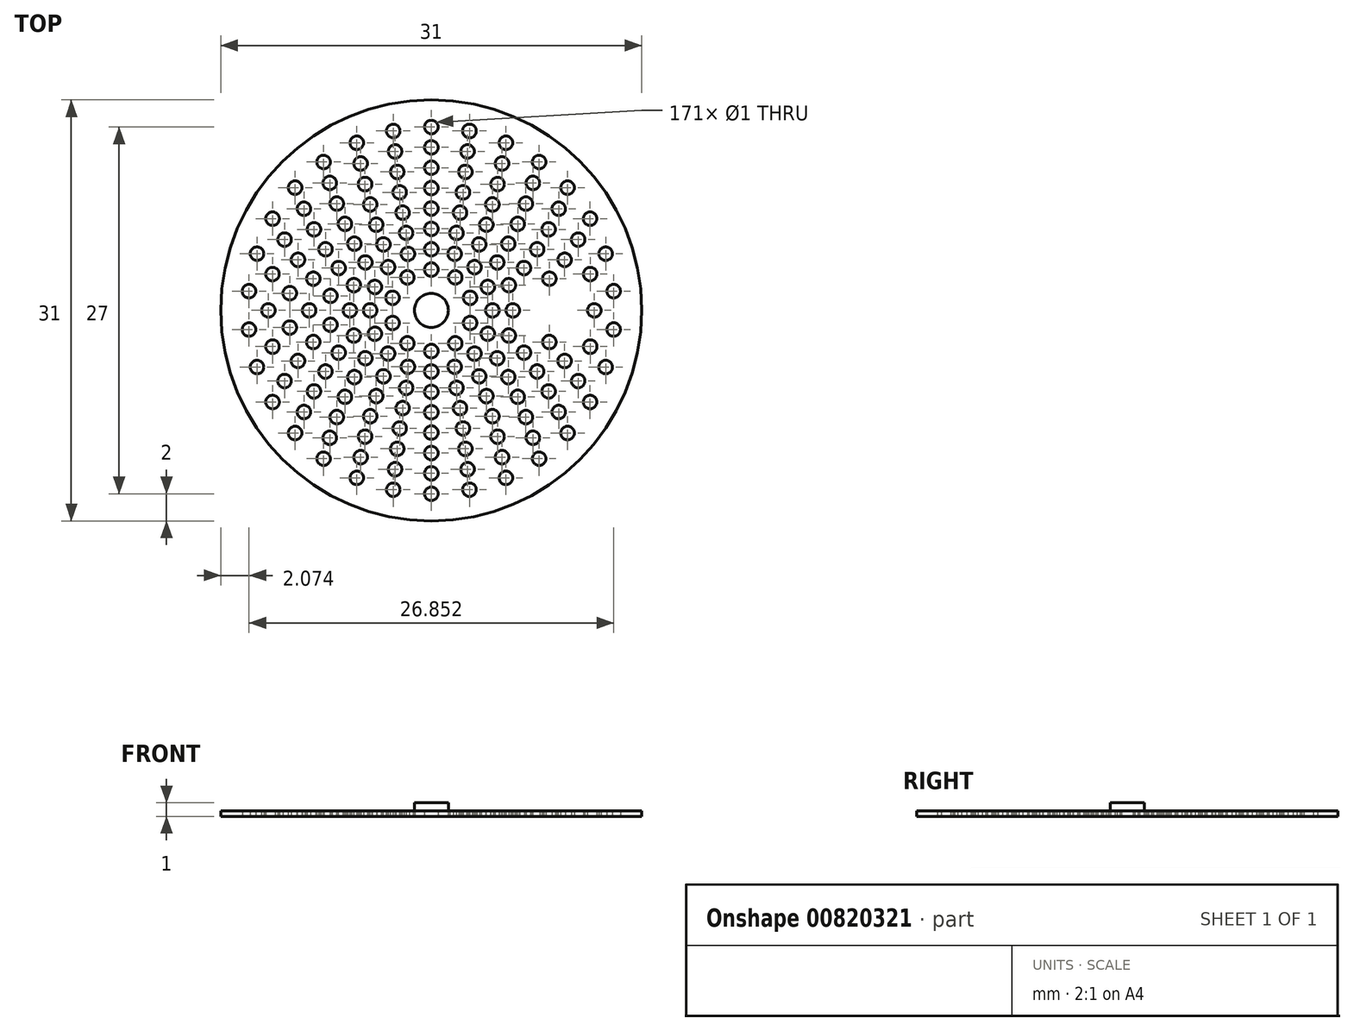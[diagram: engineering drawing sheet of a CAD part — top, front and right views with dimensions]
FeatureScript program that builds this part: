
annotation { "Feature Type Name" : "Feature", "Feature Type Description" : "" }
export const myFeature = defineFeature(function(context is Context, id is Id, definition is map)
    precondition{}
    {
        {
            var Q0;
            Q0=qCreatedBy(makeId("Top.planeOp"),FACE);
            var sketch = newSketch(context, id + "F0", { "sketchPlane" : qUnion([Q0])});
            skCircle(sketch, "E0", {"center": v(0, 0) * mm, "radius": 15.5 * mm});
            skCircle(sketch, "E1", {"center": v(0, 13.5) * mm, "radius": 0.5 * mm});
            skCircle(sketch, "E2.1.0", {"center": v(-2.8, 13.2) * mm, "radius": 0.5 * mm});
            skCircle(sketch, "E2.2.0", {"center": v(-5.5, 12.33) * mm, "radius": 0.5 * mm});
            skCircle(sketch, "E2.3.0", {"center": v(-7.94, 10.92) * mm, "radius": 0.5 * mm});
            skCircle(sketch, "E2.4.0", {"center": v(-10.03, 9.03) * mm, "radius": 0.5 * mm});
            skCircle(sketch, "E2.5.0", {"center": v(-11.7, 6.75) * mm, "radius": 0.5 * mm});
            skCircle(sketch, "E2.6.0", {"center": v(-12.84, 4.17) * mm, "radius": 0.5 * mm});
            skCircle(sketch, "E2.7.0", {"center": v(-13.43, 1.41) * mm, "radius": 0.5 * mm});
            skCircle(sketch, "E2.8.0", {"center": v(-13.43, -1.41) * mm, "radius": 0.5 * mm});
            skCircle(sketch, "E2.9.0", {"center": v(-12.84, -4.17) * mm, "radius": 0.5 * mm});
            skCircle(sketch, "E2.10.0", {"center": v(-11.7, -6.75) * mm, "radius": 0.5 * mm});
            skCircle(sketch, "E2.11.0", {"center": v(-10.03, -9.03) * mm, "radius": 0.5 * mm});
            skCircle(sketch, "E2.12.0", {"center": v(-7.94, -10.92) * mm, "radius": 0.5 * mm});
            skCircle(sketch, "E2.13.0", {"center": v(-5.5, -12.33) * mm, "radius": 0.5 * mm});
            skCircle(sketch, "E2.14.0", {"center": v(-2.8, -13.2) * mm, "radius": 0.5 * mm});
            skCircle(sketch, "E2.15.0", {"center": v(0, -13.5) * mm, "radius": 0.5 * mm});
            skCircle(sketch, "E2.16.0", {"center": v(2.8, -13.2) * mm, "radius": 0.5 * mm});
            skCircle(sketch, "E2.17.0", {"center": v(5.5, -12.33) * mm, "radius": 0.5 * mm});
            skCircle(sketch, "E2.18.0", {"center": v(7.94, -10.92) * mm, "radius": 0.5 * mm});
            skCircle(sketch, "E2.19.0", {"center": v(10.03, -9.03) * mm, "radius": 0.5 * mm});
            skCircle(sketch, "E2.20.0", {"center": v(11.7, -6.75) * mm, "radius": 0.5 * mm});
            skCircle(sketch, "E2.21.0", {"center": v(12.84, -4.17) * mm, "radius": 0.5 * mm});
            skCircle(sketch, "E2.22.0", {"center": v(13.43, -1.41) * mm, "radius": 0.5 * mm});
            skCircle(sketch, "E2.23.0", {"center": v(13.43, 1.41) * mm, "radius": 0.5 * mm});
            skCircle(sketch, "E2.24.0", {"center": v(12.84, 4.17) * mm, "radius": 0.5 * mm});
            skCircle(sketch, "E2.25.0", {"center": v(11.7, 6.75) * mm, "radius": 0.5 * mm});
            skCircle(sketch, "E2.26.0", {"center": v(10.03, 9.03) * mm, "radius": 0.5 * mm});
            skCircle(sketch, "E2.27.0", {"center": v(7.94, 10.92) * mm, "radius": 0.5 * mm});
            skCircle(sketch, "E2.28.0", {"center": v(5.5, 12.33) * mm, "radius": 0.5 * mm});
            skCircle(sketch, "E2.29.0", {"center": v(2.8, 13.2) * mm, "radius": 0.5 * mm});
            skCircle(sketch, "E3", {"center": v(0, 0) * mm, "radius": 1.25 * mm});
            skCircle(sketch, "E4", {"center": v(0, 12) * mm, "radius": 0.5 * mm});
            skCircle(sketch, "E5", {"center": v(0, 10.5) * mm, "radius": 0.5 * mm});
            skCircle(sketch, "E6", {"center": v(0, 9) * mm, "radius": 0.5 * mm});
            skCircle(sketch, "E7", {"center": v(0, 7.5) * mm, "radius": 0.5 * mm});
            skCircle(sketch, "E8", {"center": v(0, 6) * mm, "radius": 0.5 * mm});
            skCircle(sketch, "E9", {"center": v(0, 4.5) * mm, "radius": 0.5 * mm});
            skCircle(sketch, "E10", {"center": v(0, 3) * mm, "radius": 0.5 * mm});
            skCircle(sketch, "E11.1.0", {"center": v(-2.67, 11.7) * mm, "radius": 0.5 * mm});
            skCircle(sketch, "E11.2.0", {"center": v(-5.2, 10.81) * mm, "radius": 0.5 * mm});
            skCircle(sketch, "E12.1.3.0", {"center": v(-7.48, 9.38) * mm, "radius": 0.5 * mm});
            skCircle(sketch, "E12.1.4.0", {"center": v(-9.38, 7.48) * mm, "radius": 0.5 * mm});
            skCircle(sketch, "E12.1.5.0", {"center": v(-10.81, 5.2) * mm, "radius": 0.5 * mm});
            skCircle(sketch, "E12.1.6.0", {"center": v(-11.7, 2.67) * mm, "radius": 0.5 * mm});
            skCircle(sketch, "E12.1.7.0", {"center": v(-12, 0) * mm, "radius": 0.5 * mm});
            skCircle(sketch, "E12.1.8.0", {"center": v(-11.7, -2.67) * mm, "radius": 0.5 * mm});
            skCircle(sketch, "E12.1.9.0", {"center": v(-10.81, -5.2) * mm, "radius": 0.5 * mm});
            skCircle(sketch, "E12.1.10.0", {"center": v(-9.38, -7.48) * mm, "radius": 0.5 * mm});
            skCircle(sketch, "E12.1.11.0", {"center": v(-7.48, -9.38) * mm, "radius": 0.5 * mm});
            skCircle(sketch, "E12.1.12.0", {"center": v(-5.2, -10.81) * mm, "radius": 0.5 * mm});
            skCircle(sketch, "E12.1.13.0", {"center": v(-2.67, -11.7) * mm, "radius": 0.5 * mm});
            skCircle(sketch, "E12.1.14.0", {"center": v(0, -12) * mm, "radius": 0.5 * mm});
            skCircle(sketch, "E12.1.15.0", {"center": v(2.67, -11.7) * mm, "radius": 0.5 * mm});
            skCircle(sketch, "E12.1.16.0", {"center": v(5.2, -10.81) * mm, "radius": 0.5 * mm});
            skCircle(sketch, "E12.1.17.0", {"center": v(7.48, -9.38) * mm, "radius": 0.5 * mm});
            skCircle(sketch, "E12.1.18.0", {"center": v(9.38, -7.48) * mm, "radius": 0.5 * mm});
            skCircle(sketch, "E12.1.19.0", {"center": v(10.81, -5.2) * mm, "radius": 0.5 * mm});
            skCircle(sketch, "E12.1.20.0", {"center": v(11.7, -2.67) * mm, "radius": 0.5 * mm});
            skCircle(sketch, "E12.1.21.0", {"center": v(12, 0) * mm, "radius": 0.5 * mm});
            skCircle(sketch, "E12.1.22.0", {"center": v(11.7, 2.67) * mm, "radius": 0.5 * mm});
            skCircle(sketch, "E12.1.23.0", {"center": v(10.81, 5.2) * mm, "radius": 0.5 * mm});
            skCircle(sketch, "E12.1.24.0", {"center": v(9.38, 7.48) * mm, "radius": 0.5 * mm});
            skCircle(sketch, "E12.1.25.0", {"center": v(7.48, 9.38) * mm, "radius": 0.5 * mm});
            skCircle(sketch, "E12.1.26.0", {"center": v(5.2, 10.81) * mm, "radius": 0.5 * mm});
            skCircle(sketch, "E12.1.27.0", {"center": v(2.67, 11.7) * mm, "radius": 0.5 * mm});
            skCircle(sketch, "E13.1.0", {"center": v(-2.51, 10.2) * mm, "radius": 0.5 * mm});
            skCircle(sketch, "E13.2.0", {"center": v(-4.88, 9.3) * mm, "radius": 0.5 * mm});
            skCircle(sketch, "E13.3.0", {"center": v(-6.96, 7.86) * mm, "radius": 0.5 * mm});
            skCircle(sketch, "E13.4.0", {"center": v(-8.64, 5.96) * mm, "radius": 0.5 * mm});
            skCircle(sketch, "E13.5.0", {"center": v(-9.82, 3.72) * mm, "radius": 0.5 * mm});
            skCircle(sketch, "E13.6.0", {"center": v(-10.42, 1.27) * mm, "radius": 0.5 * mm});
            skCircle(sketch, "E13.7.0", {"center": v(-10.42, -1.27) * mm, "radius": 0.5 * mm});
            skCircle(sketch, "E13.8.0", {"center": v(-9.82, -3.72) * mm, "radius": 0.5 * mm});
            skCircle(sketch, "E13.9.0", {"center": v(-8.64, -5.96) * mm, "radius": 0.5 * mm});
            skCircle(sketch, "E13.10.0", {"center": v(-6.96, -7.86) * mm, "radius": 0.5 * mm});
            skCircle(sketch, "E13.11.0", {"center": v(-4.88, -9.3) * mm, "radius": 0.5 * mm});
            skCircle(sketch, "E13.12.0", {"center": v(-2.51, -10.2) * mm, "radius": 0.5 * mm});
            skCircle(sketch, "E13.13.0", {"center": v(0, -10.5) * mm, "radius": 0.5 * mm});
            skCircle(sketch, "E13.14.0", {"center": v(2.51, -10.2) * mm, "radius": 0.5 * mm});
            skCircle(sketch, "E13.15.0", {"center": v(4.88, -9.3) * mm, "radius": 0.5 * mm});
            skCircle(sketch, "E13.16.0", {"center": v(6.96, -7.86) * mm, "radius": 0.5 * mm});
            skCircle(sketch, "E13.17.0", {"center": v(8.64, -5.96) * mm, "radius": 0.5 * mm});
            skCircle(sketch, "E13.18.0", {"center": v(9.82, -3.72) * mm, "radius": 0.5 * mm});
            skCircle(sketch, "E13.21.0", {"center": v(9.82, 3.72) * mm, "radius": 0.5 * mm});
            skCircle(sketch, "E13.22.0", {"center": v(8.64, 5.96) * mm, "radius": 0.5 * mm});
            skCircle(sketch, "E13.23.0", {"center": v(6.96, 7.86) * mm, "radius": 0.5 * mm});
            skCircle(sketch, "E13.24.0", {"center": v(4.88, 9.3) * mm, "radius": 0.5 * mm});
            skCircle(sketch, "E13.25.0", {"center": v(2.51, 10.2) * mm, "radius": 0.5 * mm});
            skCircle(sketch, "E14.1.0", {"center": v(-2.33, 8.7) * mm, "radius": 0.5 * mm});
            skCircle(sketch, "E14.2.0", {"center": v(-4.5, 7.8) * mm, "radius": 0.5 * mm});
            skCircle(sketch, "E15.1.3.0", {"center": v(-6.36, 6.36) * mm, "radius": 0.5 * mm});
            skCircle(sketch, "E15.1.4.0", {"center": v(-7.8, 4.5) * mm, "radius": 0.5 * mm});
            skCircle(sketch, "E15.1.5.0", {"center": v(-8.7, 2.33) * mm, "radius": 0.5 * mm});
            skCircle(sketch, "E15.1.6.0", {"center": v(-9, 0) * mm, "radius": 0.5 * mm});
            skCircle(sketch, "E15.1.7.0", {"center": v(-8.7, -2.33) * mm, "radius": 0.5 * mm});
            skCircle(sketch, "E15.1.8.0", {"center": v(-7.8, -4.5) * mm, "radius": 0.5 * mm});
            skCircle(sketch, "E15.1.9.0", {"center": v(-6.36, -6.36) * mm, "radius": 0.5 * mm});
            skCircle(sketch, "E15.1.10.0", {"center": v(-4.5, -7.8) * mm, "radius": 0.5 * mm});
            skCircle(sketch, "E15.1.11.0", {"center": v(-2.33, -8.7) * mm, "radius": 0.5 * mm});
            skCircle(sketch, "E15.1.12.0", {"center": v(0, -9) * mm, "radius": 0.5 * mm});
            skCircle(sketch, "E15.1.13.0", {"center": v(2.33, -8.7) * mm, "radius": 0.5 * mm});
            skCircle(sketch, "E15.1.14.0", {"center": v(4.5, -7.8) * mm, "radius": 0.5 * mm});
            skCircle(sketch, "E15.1.15.0", {"center": v(6.36, -6.36) * mm, "radius": 0.5 * mm});
            skCircle(sketch, "E15.1.16.0", {"center": v(7.8, -4.5) * mm, "radius": 0.5 * mm});
            skCircle(sketch, "E15.1.17.0", {"center": v(8.7, -2.33) * mm, "radius": 0.5 * mm});
            skCircle(sketch, "E15.1.19.0", {"center": v(8.7, 2.33) * mm, "radius": 0.5 * mm});
            skCircle(sketch, "E15.1.20.0", {"center": v(7.8, 4.5) * mm, "radius": 0.5 * mm});
            skCircle(sketch, "E15.1.21.0", {"center": v(6.36, 6.36) * mm, "radius": 0.5 * mm});
            skCircle(sketch, "E15.1.22.0", {"center": v(4.5, 7.8) * mm, "radius": 0.5 * mm});
            skCircle(sketch, "E15.1.23.0", {"center": v(2.33, 8.7) * mm, "radius": 0.5 * mm});
            skCircle(sketch, "E16.1.0", {"center": v(-2.11, 7.2) * mm, "radius": 0.5 * mm});
            skCircle(sketch, "E16.2.0", {"center": v(-4.05, 6.3) * mm, "radius": 0.5 * mm});
            skCircle(sketch, "E17.1.3.0", {"center": v(-5.67, 4.91) * mm, "radius": 0.5 * mm});
            skCircle(sketch, "E17.1.4.0", {"center": v(-6.82, 3.12) * mm, "radius": 0.5 * mm});
            skCircle(sketch, "E17.1.5.0", {"center": v(-7.42, 1.07) * mm, "radius": 0.5 * mm});
            skCircle(sketch, "E17.1.6.0", {"center": v(-7.42, -1.07) * mm, "radius": 0.5 * mm});
            skCircle(sketch, "E17.1.7.0", {"center": v(-6.82, -3.12) * mm, "radius": 0.5 * mm});
            skCircle(sketch, "E17.1.8.0", {"center": v(-5.67, -4.91) * mm, "radius": 0.5 * mm});
            skCircle(sketch, "E17.1.9.0", {"center": v(-4.05, -6.3) * mm, "radius": 0.5 * mm});
            skCircle(sketch, "E17.1.10.0", {"center": v(-2.11, -7.2) * mm, "radius": 0.5 * mm});
            skCircle(sketch, "E17.1.11.0", {"center": v(0, -7.5) * mm, "radius": 0.5 * mm});
            skCircle(sketch, "E17.1.12.0", {"center": v(2.11, -7.2) * mm, "radius": 0.5 * mm});
            skCircle(sketch, "E17.1.13.0", {"center": v(4.05, -6.3) * mm, "radius": 0.5 * mm});
            skCircle(sketch, "E17.1.14.0", {"center": v(5.67, -4.91) * mm, "radius": 0.5 * mm});
            skCircle(sketch, "E17.1.15.0", {"center": v(6.82, -3.12) * mm, "radius": 0.5 * mm});
            skCircle(sketch, "E17.1.18.0", {"center": v(6.82, 3.12) * mm, "radius": 0.5 * mm});
            skCircle(sketch, "E17.1.19.0", {"center": v(5.67, 4.91) * mm, "radius": 0.5 * mm});
            skCircle(sketch, "E17.1.20.0", {"center": v(4.05, 6.3) * mm, "radius": 0.5 * mm});
            skCircle(sketch, "E17.1.21.0", {"center": v(2.11, 7.2) * mm, "radius": 0.5 * mm});
            skCircle(sketch, "E18.1.0", {"center": v(-1.85, 5.7) * mm, "radius": 0.5 * mm});
            skCircle(sketch, "E18.2.0", {"center": v(-3.53, 4.85) * mm, "radius": 0.5 * mm});
            skCircle(sketch, "E18.3.0", {"center": v(-4.85, 3.53) * mm, "radius": 0.5 * mm});
            skCircle(sketch, "E18.4.0", {"center": v(-5.7, 1.85) * mm, "radius": 0.5 * mm});
            skCircle(sketch, "E18.5.0", {"center": v(-6, 0) * mm, "radius": 0.5 * mm});
            skCircle(sketch, "E18.6.0", {"center": v(-5.7, -1.85) * mm, "radius": 0.5 * mm});
            skCircle(sketch, "E18.7.0", {"center": v(-4.85, -3.53) * mm, "radius": 0.5 * mm});
            skCircle(sketch, "E18.8.0", {"center": v(-3.53, -4.85) * mm, "radius": 0.5 * mm});
            skCircle(sketch, "E18.9.0", {"center": v(-1.85, -5.7) * mm, "radius": 0.5 * mm});
            skCircle(sketch, "E18.10.0", {"center": v(0, -6) * mm, "radius": 0.5 * mm});
            skCircle(sketch, "E18.11.0", {"center": v(1.85, -5.7) * mm, "radius": 0.5 * mm});
            skCircle(sketch, "E18.12.0", {"center": v(3.53, -4.85) * mm, "radius": 0.5 * mm});
            skCircle(sketch, "E18.13.0", {"center": v(4.85, -3.53) * mm, "radius": 0.5 * mm});
            skCircle(sketch, "E18.14.0", {"center": v(5.7, -1.85) * mm, "radius": 0.5 * mm});
            skCircle(sketch, "E18.15.0", {"center": v(6, 0) * mm, "radius": 0.5 * mm});
            skCircle(sketch, "E18.16.0", {"center": v(5.7, 1.85) * mm, "radius": 0.5 * mm});
            skCircle(sketch, "E18.17.0", {"center": v(4.85, 3.53) * mm, "radius": 0.5 * mm});
            skCircle(sketch, "E18.18.0", {"center": v(3.53, 4.85) * mm, "radius": 0.5 * mm});
            skCircle(sketch, "E18.19.0", {"center": v(1.85, 5.7) * mm, "radius": 0.5 * mm});
            skCircle(sketch, "E19.1.0", {"center": v(-1.72, 4.16) * mm, "radius": 0.5 * mm});
            skCircle(sketch, "E19.2.0", {"center": v(-3.18, 3.18) * mm, "radius": 0.5 * mm});
            skCircle(sketch, "E19.3.0", {"center": v(-4.16, 1.72) * mm, "radius": 0.5 * mm});
            skCircle(sketch, "E19.4.0", {"center": v(-4.5, 0) * mm, "radius": 0.5 * mm});
            skCircle(sketch, "E19.5.0", {"center": v(-4.16, -1.72) * mm, "radius": 0.5 * mm});
            skCircle(sketch, "E19.6.0", {"center": v(-3.18, -3.18) * mm, "radius": 0.5 * mm});
            skCircle(sketch, "E19.7.0", {"center": v(-1.72, -4.16) * mm, "radius": 0.5 * mm});
            skCircle(sketch, "E19.8.0", {"center": v(0, -4.5) * mm, "radius": 0.5 * mm});
            skCircle(sketch, "E19.9.0", {"center": v(1.72, -4.16) * mm, "radius": 0.5 * mm});
            skCircle(sketch, "E19.10.0", {"center": v(3.18, -3.18) * mm, "radius": 0.5 * mm});
            skCircle(sketch, "E19.11.0", {"center": v(4.16, -1.72) * mm, "radius": 0.5 * mm});
            skCircle(sketch, "E19.12.0", {"center": v(4.5, 0) * mm, "radius": 0.5 * mm});
            skCircle(sketch, "E19.13.0", {"center": v(4.16, 1.72) * mm, "radius": 0.5 * mm});
            skCircle(sketch, "E19.14.0", {"center": v(3.18, 3.18) * mm, "radius": 0.5 * mm});
            skCircle(sketch, "E19.15.0", {"center": v(1.72, 4.16) * mm, "radius": 0.5 * mm});
            skCircle(sketch, "E20.1.0", {"center": v(-1.76, 2.43) * mm, "radius": 0.5 * mm});
            skCircle(sketch, "E20.2.0", {"center": v(-2.85, 0.93) * mm, "radius": 0.5 * mm});
            skCircle(sketch, "E20.3.0", {"center": v(-2.85, -0.93) * mm, "radius": 0.5 * mm});
            skCircle(sketch, "E20.4.0", {"center": v(-1.76, -2.43) * mm, "radius": 0.5 * mm});
            skCircle(sketch, "E20.5.0", {"center": v(0, -3) * mm, "radius": 0.5 * mm});
            skCircle(sketch, "E20.6.0", {"center": v(1.76, -2.43) * mm, "radius": 0.5 * mm});
            skCircle(sketch, "E20.7.0", {"center": v(2.85, -0.93) * mm, "radius": 0.5 * mm});
            skCircle(sketch, "E20.8.0", {"center": v(2.85, 0.93) * mm, "radius": 0.5 * mm});
            skCircle(sketch, "E20.9.0", {"center": v(1.76, 2.43) * mm, "radius": 0.5 * mm});
            skSolve(sketch);
        }
        {
            var Q0;
            Q0=qSketchRegion(id+"F0",true);
            extrude(context, id + "F1", {"entities" : qUnion([Q0]), "depth" : 0.4 * mm, "offsetDistance" : 25 * mm});
        }
        {
            var Q0;
            Q0=makeQuery(id+"F1.opExtrude","CAP_FACE",FACE,{"disambiguationData":[OSD([sQuery(id+"F0.wireOp",EDGE,"E0"),sQuery(id+"F0.wireOp",EDGE,"E1"),sQuery(id+"F0.wireOp",EDGE,"E2.1.0"),sQuery(id+"F0.wireOp",EDGE,"E2.2.0"),sQuery(id+"F0.wireOp",EDGE,"E2.3.0"),sQuery(id+"F0.wireOp",EDGE,"E2.4.0"),sQuery(id+"F0.wireOp",EDGE,"E2.5.0"),sQuery(id+"F0.wireOp",EDGE,"E2.6.0"),sQuery(id+"F0.wireOp",EDGE,"E2.7.0"),sQuery(id+"F0.wireOp",EDGE,"E2.8.0"),sQuery(id+"F0.wireOp",EDGE,"E2.9.0"),sQuery(id+"F0.wireOp",EDGE,"E2.10.0"),sQuery(id+"F0.wireOp",EDGE,"E2.11.0"),sQuery(id+"F0.wireOp",EDGE,"E2.12.0"),sQuery(id+"F0.wireOp",EDGE,"E2.13.0"),sQuery(id+"F0.wireOp",EDGE,"E2.14.0"),sQuery(id+"F0.wireOp",EDGE,"E2.15.0"),sQuery(id+"F0.wireOp",EDGE,"E2.16.0"),sQuery(id+"F0.wireOp",EDGE,"E2.17.0"),sQuery(id+"F0.wireOp",EDGE,"E2.18.0"),sQuery(id+"F0.wireOp",EDGE,"E2.19.0"),sQuery(id+"F0.wireOp",EDGE,"E2.20.0"),sQuery(id+"F0.wireOp",EDGE,"E2.21.0"),sQuery(id+"F0.wireOp",EDGE,"E2.22.0"),sQuery(id+"F0.wireOp",EDGE,"E2.23.0"),sQuery(id+"F0.wireOp",EDGE,"E2.24.0"),sQuery(id+"F0.wireOp",EDGE,"E2.25.0"),sQuery(id+"F0.wireOp",EDGE,"E2.26.0"),sQuery(id+"F0.wireOp",EDGE,"E2.27.0"),sQuery(id+"F0.wireOp",EDGE,"E2.28.0"),sQuery(id+"F0.wireOp",EDGE,"E2.29.0"),sQuery(id+"F0.wireOp",EDGE,"E3"),sQuery(id+"F0.wireOp",EDGE,"E4"),sQuery(id+"F0.wireOp",EDGE,"E5"),sQuery(id+"F0.wireOp",EDGE,"E6"),sQuery(id+"F0.wireOp",EDGE,"E7"),sQuery(id+"F0.wireOp",EDGE,"E8"),sQuery(id+"F0.wireOp",EDGE,"E9"),sQuery(id+"F0.wireOp",EDGE,"E10"),sQuery(id+"F0.wireOp",EDGE,"E11.1.0"),sQuery(id+"F0.wireOp",EDGE,"E11.2.0"),sQuery(id+"F0.wireOp",EDGE,"E12.1.3.0"),sQuery(id+"F0.wireOp",EDGE,"E12.1.4.0"),sQuery(id+"F0.wireOp",EDGE,"E12.1.5.0"),sQuery(id+"F0.wireOp",EDGE,"E12.1.6.0"),sQuery(id+"F0.wireOp",EDGE,"E12.1.7.0"),sQuery(id+"F0.wireOp",EDGE,"E12.1.8.0"),sQuery(id+"F0.wireOp",EDGE,"E12.1.9.0"),sQuery(id+"F0.wireOp",EDGE,"E12.1.10.0"),sQuery(id+"F0.wireOp",EDGE,"E12.1.11.0"),sQuery(id+"F0.wireOp",EDGE,"E12.1.12.0"),sQuery(id+"F0.wireOp",EDGE,"E12.1.13.0"),sQuery(id+"F0.wireOp",EDGE,"E12.1.14.0"),sQuery(id+"F0.wireOp",EDGE,"E12.1.15.0"),sQuery(id+"F0.wireOp",EDGE,"E12.1.16.0"),sQuery(id+"F0.wireOp",EDGE,"E12.1.17.0"),sQuery(id+"F0.wireOp",EDGE,"E12.1.18.0"),sQuery(id+"F0.wireOp",EDGE,"E12.1.19.0"),sQuery(id+"F0.wireOp",EDGE,"E12.1.20.0"),sQuery(id+"F0.wireOp",EDGE,"E12.1.21.0"),sQuery(id+"F0.wireOp",EDGE,"E12.1.22.0"),sQuery(id+"F0.wireOp",EDGE,"E12.1.23.0"),sQuery(id+"F0.wireOp",EDGE,"E12.1.24.0"),sQuery(id+"F0.wireOp",EDGE,"E12.1.25.0"),sQuery(id+"F0.wireOp",EDGE,"E12.1.26.0"),sQuery(id+"F0.wireOp",EDGE,"E12.1.27.0"),sQuery(id+"F0.wireOp",EDGE,"E13.1.0"),sQuery(id+"F0.wireOp",EDGE,"E13.2.0"),sQuery(id+"F0.wireOp",EDGE,"E13.3.0"),sQuery(id+"F0.wireOp",EDGE,"E13.4.0"),sQuery(id+"F0.wireOp",EDGE,"E13.5.0"),sQuery(id+"F0.wireOp",EDGE,"E13.6.0"),sQuery(id+"F0.wireOp",EDGE,"E13.7.0"),sQuery(id+"F0.wireOp",EDGE,"E13.8.0"),sQuery(id+"F0.wireOp",EDGE,"E13.9.0"),sQuery(id+"F0.wireOp",EDGE,"E13.10.0"),sQuery(id+"F0.wireOp",EDGE,"E13.11.0"),sQuery(id+"F0.wireOp",EDGE,"E13.12.0"),sQuery(id+"F0.wireOp",EDGE,"E13.13.0"),sQuery(id+"F0.wireOp",EDGE,"E13.14.0"),sQuery(id+"F0.wireOp",EDGE,"E13.15.0"),sQuery(id+"F0.wireOp",EDGE,"E13.16.0"),sQuery(id+"F0.wireOp",EDGE,"E13.17.0"),sQuery(id+"F0.wireOp",EDGE,"E13.18.0"),sQuery(id+"F0.wireOp",EDGE,"E13.19.0"),sQuery(id+"F0.wireOp",EDGE,"E13.20.0"),sQuery(id+"F0.wireOp",EDGE,"E13.21.0"),sQuery(id+"F0.wireOp",EDGE,"E13.22.0"),sQuery(id+"F0.wireOp",EDGE,"E13.23.0"),sQuery(id+"F0.wireOp",EDGE,"E13.24.0"),sQuery(id+"F0.wireOp",EDGE,"E13.25.0"),sQuery(id+"F0.wireOp",EDGE,"E14.1.0"),sQuery(id+"F0.wireOp",EDGE,"E14.2.0"),sQuery(id+"F0.wireOp",EDGE,"E15.1.3.0"),sQuery(id+"F0.wireOp",EDGE,"E15.1.4.0"),sQuery(id+"F0.wireOp",EDGE,"E15.1.5.0"),sQuery(id+"F0.wireOp",EDGE,"E15.1.6.0"),sQuery(id+"F0.wireOp",EDGE,"E15.1.7.0"),sQuery(id+"F0.wireOp",EDGE,"E15.1.8.0"),sQuery(id+"F0.wireOp",EDGE,"E15.1.9.0"),sQuery(id+"F0.wireOp",EDGE,"E15.1.10.0"),sQuery(id+"F0.wireOp",EDGE,"E15.1.11.0"),sQuery(id+"F0.wireOp",EDGE,"E15.1.12.0"),sQuery(id+"F0.wireOp",EDGE,"E15.1.13.0"),sQuery(id+"F0.wireOp",EDGE,"E15.1.14.0"),sQuery(id+"F0.wireOp",EDGE,"E15.1.15.0"),sQuery(id+"F0.wireOp",EDGE,"E15.1.16.0"),sQuery(id+"F0.wireOp",EDGE,"E15.1.17.0"),sQuery(id+"F0.wireOp",EDGE,"E15.1.18.0"),sQuery(id+"F0.wireOp",EDGE,"E15.1.19.0"),sQuery(id+"F0.wireOp",EDGE,"E15.1.20.0"),sQuery(id+"F0.wireOp",EDGE,"E15.1.21.0"),sQuery(id+"F0.wireOp",EDGE,"E15.1.22.0"),sQuery(id+"F0.wireOp",EDGE,"E15.1.23.0"),sQuery(id+"F0.wireOp",EDGE,"E16.1.0"),sQuery(id+"F0.wireOp",EDGE,"E16.2.0"),sQuery(id+"F0.wireOp",EDGE,"E17.1.3.0"),sQuery(id+"F0.wireOp",EDGE,"E17.1.4.0"),sQuery(id+"F0.wireOp",EDGE,"E17.1.5.0"),sQuery(id+"F0.wireOp",EDGE,"E17.1.6.0"),sQuery(id+"F0.wireOp",EDGE,"E17.1.7.0"),sQuery(id+"F0.wireOp",EDGE,"E17.1.8.0"),sQuery(id+"F0.wireOp",EDGE,"E17.1.9.0"),sQuery(id+"F0.wireOp",EDGE,"E17.1.10.0"),sQuery(id+"F0.wireOp",EDGE,"E17.1.11.0"),sQuery(id+"F0.wireOp",EDGE,"E17.1.12.0"),sQuery(id+"F0.wireOp",EDGE,"E17.1.13.0"),sQuery(id+"F0.wireOp",EDGE,"E17.1.14.0"),sQuery(id+"F0.wireOp",EDGE,"E17.1.15.0"),sQuery(id+"F0.wireOp",EDGE,"E17.1.16.0"),sQuery(id+"F0.wireOp",EDGE,"E17.1.17.0"),sQuery(id+"F0.wireOp",EDGE,"E17.1.18.0"),sQuery(id+"F0.wireOp",EDGE,"E17.1.19.0"),sQuery(id+"F0.wireOp",EDGE,"E17.1.20.0"),sQuery(id+"F0.wireOp",EDGE,"E17.1.21.0"),sQuery(id+"F0.wireOp",EDGE,"E18.1.0"),sQuery(id+"F0.wireOp",EDGE,"E18.2.0"),sQuery(id+"F0.wireOp",EDGE,"E18.3.0"),sQuery(id+"F0.wireOp",EDGE,"E18.4.0"),sQuery(id+"F0.wireOp",EDGE,"E18.5.0"),sQuery(id+"F0.wireOp",EDGE,"E18.6.0"),sQuery(id+"F0.wireOp",EDGE,"E18.7.0"),sQuery(id+"F0.wireOp",EDGE,"E18.8.0"),sQuery(id+"F0.wireOp",EDGE,"E18.9.0"),sQuery(id+"F0.wireOp",EDGE,"E18.10.0"),sQuery(id+"F0.wireOp",EDGE,"E18.11.0"),sQuery(id+"F0.wireOp",EDGE,"E18.12.0"),sQuery(id+"F0.wireOp",EDGE,"E18.13.0"),sQuery(id+"F0.wireOp",EDGE,"E18.14.0"),sQuery(id+"F0.wireOp",EDGE,"E18.15.0"),sQuery(id+"F0.wireOp",EDGE,"E18.16.0"),sQuery(id+"F0.wireOp",EDGE,"E18.17.0"),sQuery(id+"F0.wireOp",EDGE,"E18.18.0"),sQuery(id+"F0.wireOp",EDGE,"E18.19.0"),sQuery(id+"F0.wireOp",EDGE,"E19.1.0"),sQuery(id+"F0.wireOp",EDGE,"E19.2.0"),sQuery(id+"F0.wireOp",EDGE,"E19.3.0"),sQuery(id+"F0.wireOp",EDGE,"E19.4.0"),sQuery(id+"F0.wireOp",EDGE,"E19.5.0"),sQuery(id+"F0.wireOp",EDGE,"E19.6.0"),sQuery(id+"F0.wireOp",EDGE,"E19.7.0"),sQuery(id+"F0.wireOp",EDGE,"E19.8.0"),sQuery(id+"F0.wireOp",EDGE,"E19.9.0"),sQuery(id+"F0.wireOp",EDGE,"E19.10.0"),sQuery(id+"F0.wireOp",EDGE,"E19.11.0"),sQuery(id+"F0.wireOp",EDGE,"E19.12.0"),sQuery(id+"F0.wireOp",EDGE,"E19.13.0"),sQuery(id+"F0.wireOp",EDGE,"E19.14.0"),sQuery(id+"F0.wireOp",EDGE,"E19.15.0"),sQuery(id+"F0.wireOp",EDGE,"E20.1.0"),sQuery(id+"F0.wireOp",EDGE,"E20.2.0"),sQuery(id+"F0.wireOp",EDGE,"E20.3.0"),sQuery(id+"F0.wireOp",EDGE,"E20.4.0"),sQuery(id+"F0.wireOp",EDGE,"E20.5.0"),sQuery(id+"F0.wireOp",EDGE,"E20.6.0"),sQuery(id+"F0.wireOp",EDGE,"E20.7.0"),sQuery(id+"F0.wireOp",EDGE,"E20.8.0"),sQuery(id+"F0.wireOp",EDGE,"E20.9.0")])],"isStart":false});
            var sketch = newSketch(context, id + "F2", { "sketchPlane" : qUnion([Q0])});
            skLineSegment(sketch, "E21.bottom", {"start": v(8, 1.05) * mm, "end": v(10.7, 1.05) * mm});
            skLineSegment(sketch, "E21.left", {"start": v(8, 1.05) * mm, "end": v(8, -1.05) * mm});
            skLineSegment(sketch, "E21.right", {"start": v(10.7, 1.05) * mm, "end": v(10.7, -1.05) * mm});
            skLineSegment(sketch, "E22", {"start": v(8, -1.05) * mm, "end": v(10.7, -1.05) * mm});
            skSolve(sketch);
        }
        {
            var Q0;
            Q0=makeQuery(id+"F0.imprint","IMPRINT",FACE,{"disambiguationData":[TD([[makeQuery(id+"F0.imprint","IMPRINT",EDGE,{"derivedFrom":sQuery(id+"F0.wireOp",EDGE,"E3")}),1.0]])]});
            extrude(context, id + "F3", {"entities" : qUnion([Q0]), "operationType" : NewBodyOperationType.ADD, "depth" : 1 * mm, "offsetDistance" : 25 * mm});
        }
    });
